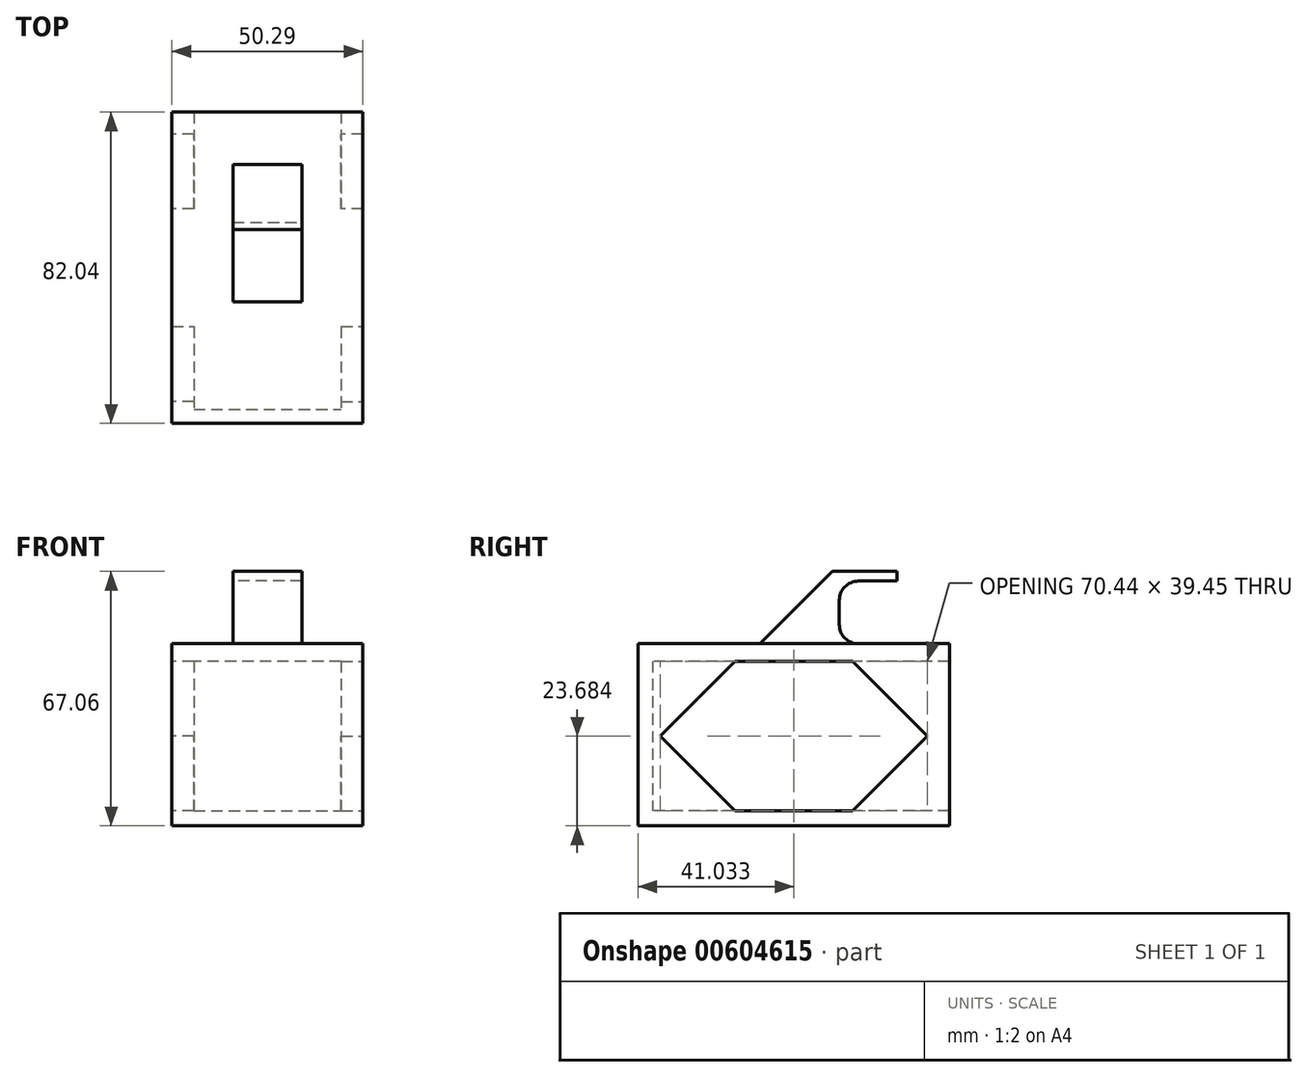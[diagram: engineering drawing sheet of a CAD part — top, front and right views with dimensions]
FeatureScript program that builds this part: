
annotation { "Feature Type Name" : "Feature", "Feature Type Description" : "" }
export const myFeature = defineFeature(function(context is Context, id is Id, definition is map)
    precondition{}
    {
        {
            var Q0;
            Q0=qCreatedBy(makeId("Top.planeOp"),FACE);
            var sketch = newSketch(context, id + "F0", { "sketchPlane" : qUnion([Q0])});
            skLineSegment(sketch, "E0.bottom", {"start": v(0, 0) * mm, "end": v(50.3, 0) * mm});
            skLineSegment(sketch, "E0.top", {"start": v(0, 82.04) * mm, "end": v(50.3, 82.04) * mm});
            skLineSegment(sketch, "E0.left", {"start": v(0, 0) * mm, "end": v(0, 82.04) * mm});
            skLineSegment(sketch, "E0.right", {"start": v(50.3, 0) * mm, "end": v(50.3, 82.04) * mm});
            skSolve(sketch);
        }
        {
            var Q0;
            Q0=makeQuery(id+"F0.imprint","IMPRINT",FACE,{"disambiguationData":[TD([[makeQuery(id+"F0.imprint","IMPRINT",EDGE,{"derivedFrom":sQuery(id+"F0.wireOp",EDGE,"E0.bottom")}),1.0]])]});
            extrude(context, id + "F1", {"entities" : qUnion([Q0]), "depth" : 48 * mm, "offsetDistance" : 25.4 * mm});
        }
        {
            var Q0;
            Q0=makeQuery(id+"F1.opExtrude","SWEPT_FACE",FACE,{"disambiguationData":[OSD([sQuery(id+"F0.wireOp",EDGE,"E0.bottom")])]});
            var sketch = newSketch(context, id + "F2", { "sketchPlane" : qUnion([Q0])});
            skLineSegment(sketch, "E1.bottom", {"start": v(5.08, 3.96) * mm, "end": v(44.54, 3.96) * mm});
            skLineSegment(sketch, "E1.top", {"start": v(5.08, 43.4) * mm, "end": v(44.54, 43.4) * mm});
            skLineSegment(sketch, "E1.left", {"start": v(5.08, 3.96) * mm, "end": v(5.08, 43.4) * mm});
            skLineSegment(sketch, "E1.right", {"start": v(44.54, 3.96) * mm, "end": v(44.54, 43.4) * mm});
            skSolve(sketch);
        }
        {
            var Q0;
            Q0=makeQuery(id+"F2.imprint","IMPRINT",FACE,{"disambiguationData":[TD([[makeQuery(id+"F2.imprint","IMPRINT",EDGE,{"derivedFrom":sQuery(id+"F2.wireOp",EDGE,"E1.bottom")}),1.0]])]});
            extrude(context, id + "F3", {"entities" : qUnion([Q0]), "operationType" : NewBodyOperationType.REMOVE, "oppositeDirection" : true, "depth" : 101.6 * mm, "offsetDistance" : 25.4 * mm});
        }
        {
            var Q0;
            Q0=makeQuery(id+"F3.boolean.opBoolean","COPY",FACE,{"derivedFrom":makeQuery(id+"F3.opExtrude","SWEPT_FACE",FACE,{"disambiguationData":[OSD([sQuery(id+"F2.wireOp",EDGE,"E1.left")])]})});
            var sketch = newSketch(context, id + "F4", { "sketchPlane" : qUnion([Q0])});
            skLineSegment(sketch, "E2.bottom", {"start": v(5.22, 3.96) * mm, "end": v(76.85, 3.96) * mm});
            skLineSegment(sketch, "E2.top", {"start": v(5.22, 43.4) * mm, "end": v(76.85, 43.4) * mm});
            skLineSegment(sketch, "E2.left", {"start": v(5.22, 3.96) * mm, "end": v(5.22, 43.4) * mm});
            skLineSegment(sketch, "E2.right", {"start": v(76.85, 3.96) * mm, "end": v(76.85, 43.4) * mm});
            skSolve(sketch);
        }
        {
            var Q0;
            Q0=makeQuery(id+"F4.imprint","IMPRINT",FACE,{"disambiguationData":[TD([[makeQuery(id+"F4.imprint","IMPRINT",EDGE,{"derivedFrom":sQuery(id+"F4.wireOp",EDGE,"E2.bottom")}),-1.0]])]});
            extrude(context, id + "F5", {"entities" : qUnion([Q0]), "operationType" : NewBodyOperationType.REMOVE, "depth" : 101.6 * mm, "offsetDistance" : 25.4 * mm, "hasSecondDirection" : true, "secondDirectionOppositeDirection" : true, "secondDirectionDepth" : 25.4 * mm});
        }
        {
            var Q0;
            {var subQ0=sQuery(id+"F4.wireOp",EDGE,"E2.bottom");var subQ1=sQuery(id+"F2.wireOp",EDGE,"E1.bottom");var subQ2=sQuery(id+"F4.wireOp",EDGE,"E2.right");Q0=makeQuery(id+"F5.boolean.opBoolean","COPY",EDGE,{"disambiguationData":[TD([makeQuery(id+"F1.opExtrude","SWEPT_FACE",FACE,{"disambiguationData":[OSD([sQuery(id+"F0.wireOp",EDGE,"E0.right")])]})])],"derivedFrom":makeQuery(id+"F5.opExtrude","SWEPT_EDGE",EDGE,{"disambiguationData":[OSD([subQ1,sQuery(id+"F2.wireOp",EDGE,"E1.left"),subQ0,subQ2])]})});}
            var Q1;
            {var subQ0=sQuery(id+"F4.wireOp",EDGE,"E2.bottom");var subQ1=sQuery(id+"F2.wireOp",EDGE,"E1.bottom");var subQ2=sQuery(id+"F4.wireOp",EDGE,"E2.left");Q1=makeQuery(id+"F5.boolean.opBoolean","COPY",EDGE,{"disambiguationData":[TD([makeQuery(id+"F1.opExtrude","SWEPT_FACE",FACE,{"disambiguationData":[OSD([sQuery(id+"F0.wireOp",EDGE,"E0.right")])]})])],"derivedFrom":makeQuery(id+"F5.opExtrude","SWEPT_EDGE",EDGE,{"disambiguationData":[OSD([subQ1,sQuery(id+"F2.wireOp",EDGE,"E1.left"),subQ0,subQ2])]})});}
            var Q2;
            {var subQ0=sQuery(id+"F4.wireOp",EDGE,"E2.top");var subQ1=sQuery(id+"F2.wireOp",EDGE,"E1.top");var subQ2=sQuery(id+"F4.wireOp",EDGE,"E2.left");Q2=makeQuery(id+"F5.boolean.opBoolean","COPY",EDGE,{"disambiguationData":[TD([makeQuery(id+"F1.opExtrude","SWEPT_FACE",FACE,{"disambiguationData":[OSD([sQuery(id+"F0.wireOp",EDGE,"E0.right")])]})])],"derivedFrom":makeQuery(id+"F5.opExtrude","SWEPT_EDGE",EDGE,{"disambiguationData":[OSD([subQ1,sQuery(id+"F2.wireOp",EDGE,"E1.left"),subQ0,subQ2])]})});}
            var Q3;
            {var subQ0=sQuery(id+"F2.wireOp",EDGE,"E1.left");var subQ1=sQuery(id+"F4.wireOp",EDGE,"E2.top");var subQ2=sQuery(id+"F2.wireOp",EDGE,"E1.top");var subQ3=sQuery(id+"F4.wireOp",EDGE,"E2.left");Q3=makeQuery(id+"F5.boolean.opBoolean","COPY",EDGE,{"disambiguationData":[TD([makeQuery(id+"F1.opExtrude","SWEPT_FACE",FACE,{"disambiguationData":[OSD([sQuery(id+"F0.wireOp",EDGE,"E0.left")])]})])],"derivedFrom":makeQuery(id+"F5.opExtrude","SWEPT_EDGE",EDGE,{"disambiguationData":[OSD([subQ2,subQ0,subQ1,subQ3])]})});}
            var Q4;
            {var subQ0=sQuery(id+"F4.wireOp",EDGE,"E2.bottom");var subQ1=sQuery(id+"F2.wireOp",EDGE,"E1.left");var subQ2=sQuery(id+"F2.wireOp",EDGE,"E1.bottom");var subQ3=sQuery(id+"F4.wireOp",EDGE,"E2.left");Q4=makeQuery(id+"F5.boolean.opBoolean","COPY",EDGE,{"disambiguationData":[TD([makeQuery(id+"F1.opExtrude","SWEPT_FACE",FACE,{"disambiguationData":[OSD([sQuery(id+"F0.wireOp",EDGE,"E0.left")])]})])],"derivedFrom":makeQuery(id+"F5.opExtrude","SWEPT_EDGE",EDGE,{"disambiguationData":[OSD([subQ2,subQ1,subQ0,subQ3])]})});}
            var Q5;
            {var subQ0=sQuery(id+"F4.wireOp",EDGE,"E2.top");var subQ1=sQuery(id+"F2.wireOp",EDGE,"E1.top");var subQ2=sQuery(id+"F4.wireOp",EDGE,"E2.right");Q5=makeQuery(id+"F5.boolean.opBoolean","COPY",EDGE,{"disambiguationData":[TD([makeQuery(id+"F1.opExtrude","SWEPT_FACE",FACE,{"disambiguationData":[OSD([sQuery(id+"F0.wireOp",EDGE,"E0.right")])]})])],"derivedFrom":makeQuery(id+"F5.opExtrude","SWEPT_EDGE",EDGE,{"disambiguationData":[OSD([subQ1,sQuery(id+"F2.wireOp",EDGE,"E1.left"),subQ0,subQ2])]})});}
            var Q6;
            {var subQ0=sQuery(id+"F2.wireOp",EDGE,"E1.left");var subQ1=sQuery(id+"F4.wireOp",EDGE,"E2.top");var subQ2=sQuery(id+"F2.wireOp",EDGE,"E1.top");var subQ3=sQuery(id+"F4.wireOp",EDGE,"E2.right");Q6=makeQuery(id+"F5.boolean.opBoolean","COPY",EDGE,{"disambiguationData":[TD([makeQuery(id+"F1.opExtrude","SWEPT_FACE",FACE,{"disambiguationData":[OSD([sQuery(id+"F0.wireOp",EDGE,"E0.left")])]})])],"derivedFrom":makeQuery(id+"F5.opExtrude","SWEPT_EDGE",EDGE,{"disambiguationData":[OSD([subQ2,subQ0,subQ1,subQ3])]})});}
            var Q7;
            {var subQ0=sQuery(id+"F4.wireOp",EDGE,"E2.bottom");var subQ1=sQuery(id+"F2.wireOp",EDGE,"E1.left");var subQ2=sQuery(id+"F2.wireOp",EDGE,"E1.bottom");var subQ3=sQuery(id+"F4.wireOp",EDGE,"E2.right");Q7=makeQuery(id+"F5.boolean.opBoolean","COPY",EDGE,{"disambiguationData":[TD([makeQuery(id+"F1.opExtrude","SWEPT_FACE",FACE,{"disambiguationData":[OSD([sQuery(id+"F0.wireOp",EDGE,"E0.left")])]})])],"derivedFrom":makeQuery(id+"F5.opExtrude","SWEPT_EDGE",EDGE,{"disambiguationData":[OSD([subQ2,subQ1,subQ0,subQ3])]})});}
            chamfer(context, id + "F6", {"entities" : qUnion([Q0, Q1, Q2, Q3, Q4, Q5, Q6, Q7]), "width" : 20.32 * mm, "tangentPropagation" : true});
        }
        {
            var Q0;
            Q0=makeQuery(id+"F1.opExtrude","CAP_FACE",FACE,{"disambiguationData":[OSD([sQuery(id+"F0.wireOp",EDGE,"E0.bottom"),sQuery(id+"F0.wireOp",EDGE,"E0.top"),sQuery(id+"F0.wireOp",EDGE,"E0.left"),sQuery(id+"F0.wireOp",EDGE,"E0.right")])],"isStart":false});
            var sketch = newSketch(context, id + "F7", { "sketchPlane" : qUnion([Q0])});
            skPoint(sketch, "E3.firstSnap0", {"position": v(25.15, 0) * mm});
            skLineSegment(sketch, "E3.bottom", {"start": v(25.15, 32.08) * mm, "end": v(29.16, 32.08) * mm});
            skLineSegment(sketch, "E3.top", {"start": v(25.15, 40.3) * mm, "end": v(29.16, 40.3) * mm});
            skLineSegment(sketch, "E3.left", {"start": v(25.15, 32.08) * mm, "end": v(25.15, 40.3) * mm});
            skLineSegment(sketch, "E3.right", {"start": v(29.16, 32.08) * mm, "end": v(29.16, 40.3) * mm});
            skSolve(sketch);
        }
        {
            var Q0;
            Q0=makeQuery(id+"F7.imprint","IMPRINT",FACE,{"disambiguationData":[TD([[makeQuery(id+"F7.imprint","IMPRINT",EDGE,{"derivedFrom":sQuery(id+"F7.wireOp",EDGE,"E3.bottom")}),1.0]])]});
            extrude(context, id + "F8", {"entities" : qUnion([Q0]), "operationType" : NewBodyOperationType.ADD, "depth" : 19.05 * mm, "offsetDistance" : 25.4 * mm});
        }
        {
            var Q0;
            Q0=makeQuery(id+"F8.opExtrude","SWEPT_FACE",FACE,{"disambiguationData":[OSD([sQuery(id+"F7.wireOp",EDGE,"E3.top")])]});
            extrude(context, id + "F9", {"entities" : qUnion([Q0]), "operationType" : NewBodyOperationType.ADD, "depth" : 12.7 * mm, "offsetDistance" : 25.4 * mm});
        }
        {
            var Q0;
            Q0=makeQuery(id+"F8.opExtrude","CAP_EDGE",EDGE,{"disambiguationData":[OSD([sQuery(id+"F7.wireOp",EDGE,"E3.bottom")])],"isStart":false});
            chamfer(context, id + "F10", {"entities" : qUnion([Q0]), "width" : 19.05 * mm, "tangentPropagation" : true});
        }
        {
            var Q0;
            {var subQ0=sQuery(id+"F7.wireOp",EDGE,"E3.right");Q0=makeQuery(id+"F9.boolean.opBoolean","MERGE",FACE,{"derivedFrom":[makeQuery(id+"F8.opExtrude","SWEPT_FACE",FACE,{"disambiguationData":[OSD([subQ0])]}),makeQuery(id+"F9.opExtrude","SWEPT_FACE",FACE,{"disambiguationData":[OSD([sQuery(id+"F7.wireOp",EDGE,"E3.top"),subQ0])]})]});}
            extrude(context, id + "F11", {"entities" : qUnion([Q0]), "operationType" : NewBodyOperationType.ADD, "depth" : 5.08 * mm, "offsetDistance" : 25.4 * mm});
        }
        {
            var Q0;
            Q0=makeQuery(id+"F1.opExtrude","SWEPT_BODY",BODY,{"disambiguationData":[OSD([sQuery(id+"F0.wireOp",EDGE,"E0.bottom"),sQuery(id+"F0.wireOp",EDGE,"E0.top"),sQuery(id+"F0.wireOp",EDGE,"E0.left"),sQuery(id+"F0.wireOp",EDGE,"E0.right")])]});
            var Q1;
            {var subQ0=sQuery(id+"F7.wireOp",EDGE,"E3.left");Q1=makeQuery(id+"F9.boolean.opBoolean","MERGE",FACE,{"derivedFrom":[makeQuery(id+"F8.opExtrude","SWEPT_FACE",FACE,{"disambiguationData":[OSD([subQ0])]}),makeQuery(id+"F9.opExtrude","SWEPT_FACE",FACE,{"disambiguationData":[OSD([sQuery(id+"F7.wireOp",EDGE,"E3.top"),subQ0])]})]});}
            mirror(context, id + "F12", {"operationType" : NewBodyOperationType.ADD, "entities" : qUnion([Q0]), "mirrorPlane" : qUnion([Q1])});
        }
        {
            var Q0;
            {var subQ0=sQuery(id+"F7.wireOp",EDGE,"E3.right");var subQ1=sQuery(id+"F7.wireOp",EDGE,"E3.top");var subQ2=makeQuery(id+"F11.boolean.opBoolean","MERGE",FACE,{"derivedFrom":[makeQuery(id+"F9.opExtrude","CAP_FACE",FACE,{"disambiguationData":[OSD([subQ1])],"isStart":false}),makeQuery(id+"F11.opExtrude","SWEPT_FACE",FACE,{"disambiguationData":[OSD([subQ1,subQ0]),TDD([makeQuery(id+"F9.opExtrude","CAP_EDGE",EDGE,{"disambiguationData":[OSD([subQ1,subQ0])],"isStart":false})])]})]});Q0=makeQuery(id+"F12.boolean.opBoolean","MERGE",FACE,{"derivedFrom":[subQ2,makeQuery(id+"F12.opPattern","COPY",FACE,{"derivedFrom":subQ2,"instanceName":"1"})]});}
            extrude(context, id + "F13", {"entities" : qUnion([Q0]), "operationType" : NewBodyOperationType.ADD, "depth" : 10.16 * mm, "offsetDistance" : 25.4 * mm});
        }
        {
            var Q0;
            Q0=makeQuery(id+"F13.opExtrude","CAP_FACE",FACE,{"disambiguationData":[OSD([sQuery(id+"F7.wireOp",EDGE,"E3.top"),sQuery(id+"F7.wireOp",EDGE,"E3.right")])],"isStart":false});
            var sketch = newSketch(context, id + "F14", { "sketchPlane" : qUnion([Q0])});
            skLineSegment(sketch, "E4.bottom", {"start": v(-34.24, 48) * mm, "end": v(-16.05, 48) * mm});
            skLineSegment(sketch, "E4.top", {"start": v(-34.24, 64.52) * mm, "end": v(-16.05, 64.52) * mm});
            skLineSegment(sketch, "E4.left", {"start": v(-34.24, 48) * mm, "end": v(-34.24, 64.52) * mm});
            skLineSegment(sketch, "E4.right", {"start": v(-16.05, 48) * mm, "end": v(-16.05, 64.52) * mm});
            skSolve(sketch);
        }
        {
            var Q0;
            Q0=makeQuery(id+"F14.imprint","IMPRINT",FACE,{"disambiguationData":[TD([[makeQuery(id+"F14.imprint","IMPRINT",EDGE,{"derivedFrom":sQuery(id+"F14.wireOp",EDGE,"E4.bottom")}),-1.0]])]});
            extrude(context, id + "F15", {"entities" : qUnion([Q0]), "operationType" : NewBodyOperationType.REMOVE, "oppositeDirection" : true, "depth" : 10.16 * mm, "offsetDistance" : 25.4 * mm});
        }
        {
            var Q0;
            Q0=makeQuery(id+"F15.boolean.opBoolean","COPY",EDGE,{"derivedFrom":makeQuery(id+"F15.opExtrude","CAP_EDGE",EDGE,{"disambiguationData":[OSD([sQuery(id+"F14.wireOp",EDGE,"E4.top")])],"isStart":false})});
            var Q1;
            Q1=makeQuery(id+"F15.boolean.opBoolean","COPY",EDGE,{"derivedFrom":makeQuery(id+"F15.opExtrude","CAP_EDGE",EDGE,{"disambiguationData":[OSD([sQuery(id+"F14.wireOp",EDGE,"E4.bottom")])],"isStart":false})});
            fillet(context, id + "F16", {"entities" : qUnion([Q0, Q1]), "radius" : 5.08 * mm, "tangentPropagation" : true, "allowEdgeOverflow" : false});
        }
        {
            var Q0;
            Q0=makeQuery(id+"F13.opExtrude","CAP_FACE",FACE,{"disambiguationData":[OSD([sQuery(id+"F7.wireOp",EDGE,"E3.top"),sQuery(id+"F7.wireOp",EDGE,"E3.right")])],"isStart":false});
            extrude(context, id + "F17", {"entities" : qUnion([Q0]), "operationType" : NewBodyOperationType.ADD, "depth" : 5.08 * mm, "offsetDistance" : 25.4 * mm});
        }
        {
            var Q0;
            Q0=makeQuery(id+"F5.boolean.opBoolean","MERGE",FACE,{"derivedFrom":[makeQuery(id+"F3.boolean.opBoolean","COPY",FACE,{"derivedFrom":makeQuery(id+"F3.opExtrude","SWEPT_FACE",FACE,{"disambiguationData":[OSD([sQuery(id+"F2.wireOp",EDGE,"E1.bottom")])]})}),makeQuery(id+"F5.opExtrude","SWEPT_FACE",FACE,{"disambiguationData":[OSD([sQuery(id+"F4.wireOp",EDGE,"E2.bottom")])]})]});
            var sketch = newSketch(context, id + "F18", { "sketchPlane" : qUnion([Q0])});
            skLineSegment(sketch, "E5.bottom", {"start": v(5.75, 0) * mm, "end": v(44.54, 0) * mm});
            skLineSegment(sketch, "E5.top", {"start": v(5.75, 3.78) * mm, "end": v(44.54, 3.78) * mm});
            skLineSegment(sketch, "E5.left", {"start": v(5.75, 0) * mm, "end": v(5.75, 3.78) * mm});
            skLineSegment(sketch, "E5.right", {"start": v(44.54, 0) * mm, "end": v(44.54, 3.78) * mm});
            skSolve(sketch);
        }
        {
            var Q0;
            Q0=makeQuery(id+"F18.imprint","IMPRINT",FACE,{"disambiguationData":[TD([[makeQuery(id+"F18.imprint","IMPRINT",EDGE,{"derivedFrom":sQuery(id+"F18.wireOp",EDGE,"E5.bottom")}),1.0]])]});
            var Q1;
            Q1=sQuery(id+"F18.wireOp",EDGE,"E5.top");
            extrude(context, id + "F19", {"entities" : qUnion([Q0]), "operationType" : NewBodyOperationType.ADD, "surfaceEntities" : qUnion([Q1]), "depth" : 40.64 * mm, "offsetDistance" : 25.4 * mm});
        }
    });
